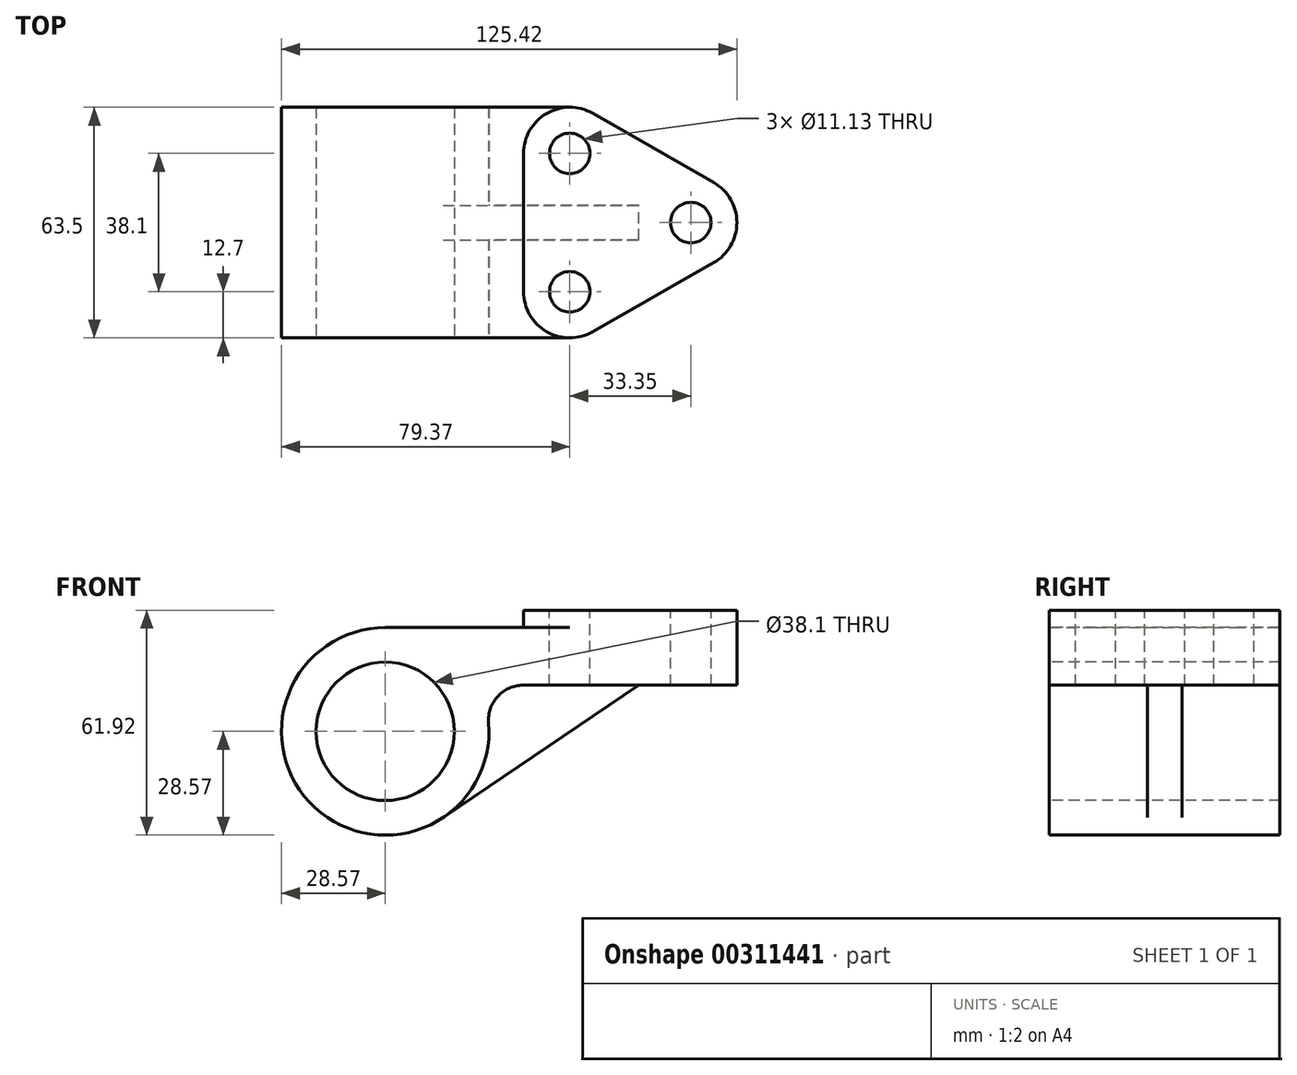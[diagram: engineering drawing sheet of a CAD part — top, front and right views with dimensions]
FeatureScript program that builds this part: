
annotation { "Feature Type Name" : "Feature", "Feature Type Description" : "" }
export const myFeature = defineFeature(function(context is Context, id is Id, definition is map)
    precondition{}
    {
        {
            var Q0;
            Q0=qCreatedBy(makeId("Front.planeOp"),FACE);
            var sketch = newSketch(context, id + "F0", { "sketchPlane" : qUnion([Q0])});
            skCircle(sketch, "E0", {"center": v(0, 0) * mm, "radius": 19.05 * mm});
            skLineSegment(sketch, "E1", {"start": v(50.8, 28.58) * mm, "end": v(50.8, 12.7) * mm});
            skLineSegment(sketch, "E2", {"start": v(50.8, 12.7) * mm, "end": v(37.97, 12.7) * mm});
            skArc(sketch, "E3", {"start": v(0, 28.58) * mm, "mid": v(-19.35, -21.03) * mm, "end": v(28.48, 2.38) * mm});
            skArc(sketch, "E4", {"start": v(37.97, 12.7) * mm, "mid": v(30.96, 9.62) * mm, "end": v(28.48, 2.38) * mm});
            skLineSegment(sketch, "E5", {"start": v(16, -23.68) * mm, "end": v(69.85, 12.7) * mm});
            skLineSegment(sketch, "E6", {"start": v(0, 28.58) * mm, "end": v(50.8, 28.58) * mm});
            skLineSegment(sketch, "E7", {"start": v(69.85, 12.7) * mm, "end": v(50.8, 12.7) * mm});
            skSolve(sketch);
        }
        {
            var Q0;
            Q0=makeQuery(id+"F0.imprint","IMPRINT",FACE,{"disambiguationData":[TD([[makeQuery(id+"F0.imprint","IMPRINT",EDGE,{"derivedFrom":sQuery(id+"F0.wireOp",EDGE,"E0")}),-1.0]])]});
            extrude(context, id + "F1", {"entities" : qUnion([Q0]), "endBound" : BoundingType.SYMMETRIC, "oppositeDirection" : true, "depth" : 63.5 * mm});
        }
        {
            var Q0;
            Q0=makeQuery(id+"F0.imprint","IMPRINT",FACE,{"disambiguationData":[TD([[makeQuery(id+"F0.imprint","IMPRINT",EDGE,{"derivedFrom":sQuery(id+"F0.wireOp",EDGE,"E2")}),1.0]])]});
            extrude(context, id + "F2", {"entities" : qUnion([Q0]), "operationType" : NewBodyOperationType.ADD, "endBound" : BoundingType.SYMMETRIC, "depth" : 9.52 * mm});
        }
        {
            var Q0;
            Q0=makeQuery(id+"F1.opExtrude","SWEPT_FACE",FACE,{"disambiguationData":[OSD([sQuery(id+"F0.wireOp",EDGE,"E6")])]});
            var sketch = newSketch(context, id + "F3", { "sketchPlane" : qUnion([Q0])});
            skLineSegment(sketch, "E8.0.0", {"start": v(0, -31.75) * mm, "end": v(50.8, -31.75) * mm});
            skLineSegment(sketch, "E8.0.1", {"start": v(50.8, -31.75) * mm, "end": v(50.8, 31.75) * mm});
            skLineSegment(sketch, "E8.0.2", {"start": v(50.8, 31.75) * mm, "end": v(0, 31.75) * mm});
            skLineSegment(sketch, "E8.0.3", {"start": v(0, 31.75) * mm, "end": v(0, -31.75) * mm});
            skLineSegment(sketch, "E9", {"start": v(38.1, 19.05) * mm, "end": v(38.1, -19.05) * mm});
            skLineSegment(sketch, "E10", {"start": v(57.1, -30.08) * mm, "end": v(90.45, -11.03) * mm});
            skLineSegment(sketch, "E11", {"start": v(57.1, 30.08) * mm, "end": v(90.45, 11.03) * mm});
            skArc(sketch, "E12", {"start": v(90.45, -11.03) * mm, "mid": v(96.85, 0) * mm, "end": v(90.45, 11.03) * mm});
            skArc(sketch, "E13", {"start": v(57.1, 30.08) * mm, "mid": v(44.42, 30.03) * mm, "end": v(38.1, 19.05) * mm});
            skArc(sketch, "E14", {"start": v(38.1, -19.05) * mm, "mid": v(44.42, -30.03) * mm, "end": v(57.1, -30.08) * mm});
            skCircle(sketch, "E15", {"center": v(50.8, 19.05) * mm, "radius": 5.56 * mm});
            skCircle(sketch, "E16", {"center": v(50.8, -19.05) * mm, "radius": 5.56 * mm});
            skCircle(sketch, "E17", {"center": v(84.15, 0) * mm, "radius": 5.56 * mm});
            skLineSegment(sketch, "E18", {"start": v(0, 0) * mm, "end": v(107, 0) * mm, "construction": true});
            skSolve(sketch);
        }
        {
            var Q0;
            {var subQ9=sQuery(id+"F3.wireOp",EDGE,"E10");Q0=makeQuery(id+"F3.imprint","IMPRINT",FACE,{"disambiguationData":[TD([[makeQuery(id+"F3.imprint","IMPRINT",EDGE,{"derivedFrom":subQ9}),1.0]])]});}
            var Q1;
            {var subQ8=sQuery(id+"F3.wireOp",EDGE,"E9");Q1=makeQuery(id+"F3.imprint","IMPRINT",FACE,{"disambiguationData":[TD([[makeQuery(id+"F3.imprint","IMPRINT",EDGE,{"derivedFrom":subQ8}),1.0]])]});}
            extrude(context, id + "F4", {"entities" : qUnion([Q0, Q1]), "operationType" : NewBodyOperationType.ADD, "oppositeDirection" : true, "depth" : 15.88 * mm, "hasSecondDirection" : true, "secondDirectionOppositeDirection" : false, "secondDirectionDepth" : 4.78 * mm});
        }
        {
            var Q0;
            Q0=makeQuery(id+"F4.boolean.opBoolean","SPLIT",FACE,{"disambiguationData":[TD([makeQuery(id+"F4.opExtrude","SWEPT_FACE",FACE,{"disambiguationData":[OSD([sQuery(id+"F3.wireOp",EDGE,"E16")])]})])],"derivedFrom":makeQuery(id+"F1.opExtrude","SWEPT_FACE",FACE,{"disambiguationData":[OSD([sQuery(id+"F0.wireOp",EDGE,"E6")])]})});
            var Q1;
            Q1=makeQuery(id+"F4.boolean.opBoolean","SPLIT",FACE,{"disambiguationData":[TD([makeQuery(id+"F4.opExtrude","SWEPT_FACE",FACE,{"disambiguationData":[OSD([sQuery(id+"F3.wireOp",EDGE,"E15")])]})])],"derivedFrom":makeQuery(id+"F1.opExtrude","SWEPT_FACE",FACE,{"disambiguationData":[OSD([sQuery(id+"F0.wireOp",EDGE,"E6")])]})});
            extrude(context, id + "F5", {"entities" : qUnion([Q0, Q1]), "operationType" : NewBodyOperationType.REMOVE, "endBound" : BoundingType.THROUGH_ALL, "oppositeDirection" : true, "depth" : 25.4 * mm});
        }
    });
